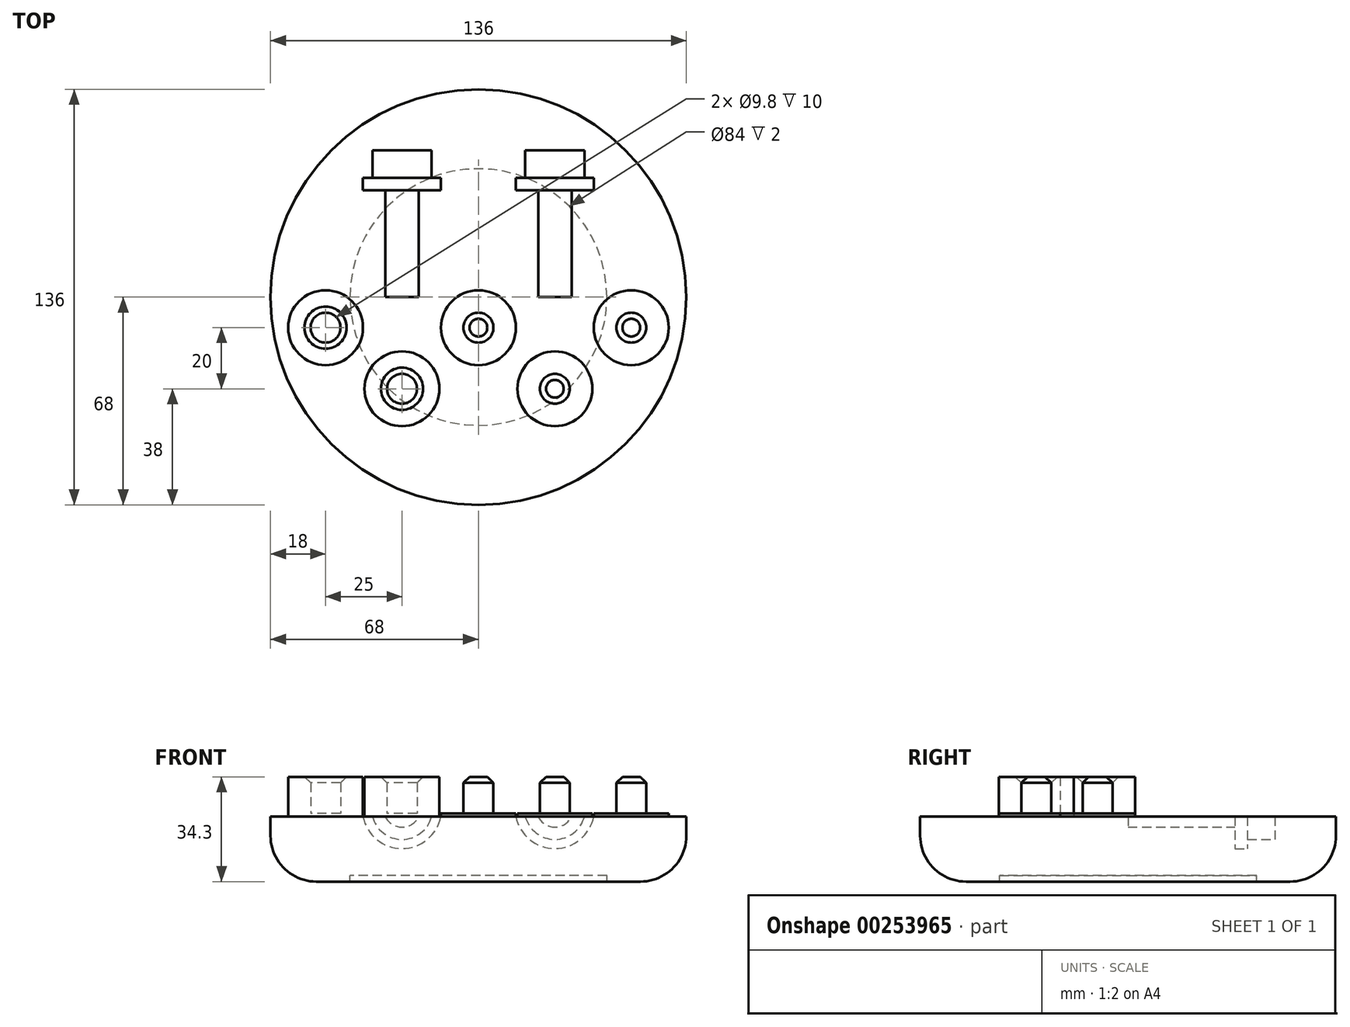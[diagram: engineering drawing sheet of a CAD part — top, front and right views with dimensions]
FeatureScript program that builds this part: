
annotation { "Feature Type Name" : "Feature", "Feature Type Description" : "" }
export const myFeature = defineFeature(function(context is Context, id is Id, definition is map)
    precondition{}
    {
        {
            var Q0;
            Q0=qCreatedBy(makeId("Front.planeOp"),FACE);
            var sketch = newSketch(context, id + "F0", { "sketchPlane" : qUnion([Q0])});
            skLineSegment(sketch, "E0.bottom", {"start": v(0, 0) * mm, "end": v(-68, 0) * mm});
            skLineSegment(sketch, "E0.top", {"start": v(-42, -21.3) * mm, "end": v(-53, -21.3) * mm});
            skLineSegment(sketch, "E0.left", {"start": v(0, 0) * mm, "end": v(0, -19.3) * mm});
            skLineSegment(sketch, "E0.right", {"start": v(-68, 0) * mm, "end": v(-68, -6.3) * mm});
            skLineSegment(sketch, "E1.top", {"start": v(0, -19.3) * mm, "end": v(-42, -19.3) * mm});
            skLineSegment(sketch, "E1.right", {"start": v(-42, -21.3) * mm, "end": v(-42, -19.3) * mm});
            skPoint(sketch, "E2.visualSharp", {"position": v(-68, -21.3) * mm});
            skArc(sketch, "E2.filletArc", {"start": v(-68, -6.3) * mm, "mid": v(-63.6, -16.9) * mm, "end": v(-53, -21.3) * mm});
            skSolve(sketch);
        }
        {
            var Q0;
            Q0=makeQuery(id+"F0.imprint","IMPRINT",FACE,{"disambiguationData":[TD([[makeQuery(id+"F0.imprint","IMPRINT",EDGE,{"derivedFrom":sQuery(id+"F0.wireOp",EDGE,"E0.bottom")}),1.0]])]});
            var Q1;
            Q1=sQuery(id+"F0.wireOp",EDGE,"E0.left");
            revolve(context, id + "F1", {"entities" : qUnion([Q0]), "axis" : qUnion([Q1]), "revolveType" : RevolveType.FULL});
        }
        {
            var Q0;
            Q0=makeQuery(id+"F1.opRevolve","SWEPT_FACE",FACE,{"disambiguationData":[OSD([sQuery(id+"F0.wireOp",EDGE,"E0.bottom")])]});
            var sketch = newSketch(context, id + "F2", { "sketchPlane" : qUnion([Q0])});
            skLineSegment(sketch, "E3.bottom", {"start": v(0, 0) * mm, "end": v(50, 0) * mm, "construction": true});
            skLineSegment(sketch, "E3.top", {"start": v(0, -10) * mm, "end": v(50, -10) * mm, "construction": true});
            skLineSegment(sketch, "E3.left", {"start": v(0, 0) * mm, "end": v(0, -10) * mm, "construction": true});
            skLineSegment(sketch, "E3.right", {"start": v(50, 0) * mm, "end": v(50, -10) * mm, "construction": true});
            skLineSegment(sketch, "E4.bottom", {"start": v(0, 0) * mm, "end": v(25, 0) * mm, "construction": true});
            skLineSegment(sketch, "E4.top", {"start": v(0, -30) * mm, "end": v(25, -30) * mm, "construction": true});
            skLineSegment(sketch, "E4.left", {"start": v(0, 0) * mm, "end": v(0, -30) * mm, "construction": true});
            skLineSegment(sketch, "E4.right", {"start": v(25, 0) * mm, "end": v(25, -30) * mm, "construction": true});
            skCircle(sketch, "E5", {"center": v(25, -30) * mm, "radius": 4.9 * mm});
            skCircle(sketch, "E6", {"center": v(50, -10) * mm, "radius": 4.9 * mm});
            skCircle(sketch, "E7", {"center": v(0, -10) * mm, "radius": 4.9 * mm});
            skCircle(sketch, "E8.MirrorC", {"center": v(-25, -30) * mm, "radius": 4.9 * mm});
            skCircle(sketch, "E9.MirrorC", {"center": v(-50, -10) * mm, "radius": 4.9 * mm});
            skCircle(sketch, "E10", {"center": v(0, -10) * mm, "radius": 12.25 * mm});
            skCircle(sketch, "E11", {"center": v(25, -30) * mm, "radius": 12.25 * mm});
            skCircle(sketch, "E12", {"center": v(50, -10) * mm, "radius": 12.25 * mm});
            skCircle(sketch, "E13", {"center": v(-25, -30) * mm, "radius": 12.25 * mm});
            skCircle(sketch, "E14", {"center": v(-50, -10) * mm, "radius": 12.25 * mm});
            skSolve(sketch);
        }
        {
            var Q0;
            Q0=makeQuery(id+"F2.imprint","IMPRINT",FACE,{"disambiguationData":[TD([[makeQuery(id+"F2.imprint","IMPRINT",EDGE,{"derivedFrom":sQuery(id+"F2.wireOp",EDGE,"E9.MirrorC")}),-1.0]])]});
            var Q1;
            Q1=makeQuery(id+"F2.imprint","IMPRINT",FACE,{"disambiguationData":[TD([[makeQuery(id+"F2.imprint","IMPRINT",EDGE,{"derivedFrom":sQuery(id+"F2.wireOp",EDGE,"E8.MirrorC")}),-1.0]])]});
            var Q2;
            Q2=makeQuery(id+"F2.imprint","IMPRINT",FACE,{"disambiguationData":[TD([[makeQuery(id+"F2.imprint","IMPRINT",EDGE,{"derivedFrom":sQuery(id+"F2.wireOp",EDGE,"E7")}),1.0]])]});
            var Q3;
            Q3=makeQuery(id+"F2.imprint","IMPRINT",FACE,{"disambiguationData":[TD([[makeQuery(id+"F2.imprint","IMPRINT",EDGE,{"derivedFrom":sQuery(id+"F2.wireOp",EDGE,"E5")}),1.0]])]});
            var Q4;
            Q4=makeQuery(id+"F2.imprint","IMPRINT",FACE,{"disambiguationData":[TD([[makeQuery(id+"F2.imprint","IMPRINT",EDGE,{"derivedFrom":sQuery(id+"F2.wireOp",EDGE,"E6")}),1.0]])]});
            extrude(context, id + "F3", {"entities" : qUnion([Q0, Q1, Q2, Q3, Q4]), "operationType" : NewBodyOperationType.ADD, "depth" : 13 * mm});
        }
        {
            var Q0;
            Q0=makeQuery(id+"F2.imprint","IMPRINT",FACE,{"disambiguationData":[TD([[makeQuery(id+"F2.imprint","IMPRINT",EDGE,{"derivedFrom":sQuery(id+"F2.wireOp",EDGE,"E9.MirrorC")}),1.0]])]});
            var Q1;
            Q1=makeQuery(id+"F2.imprint","IMPRINT",FACE,{"disambiguationData":[TD([[makeQuery(id+"F2.imprint","IMPRINT",EDGE,{"derivedFrom":sQuery(id+"F2.wireOp",EDGE,"E8.MirrorC")}),1.0]])]});
            var Q2;
            Q2=makeQuery(id+"F2.imprint","IMPRINT",FACE,{"disambiguationData":[TD([[makeQuery(id+"F2.imprint","IMPRINT",EDGE,{"derivedFrom":sQuery(id+"F2.wireOp",EDGE,"E7")}),-1.0]])]});
            var Q3;
            Q3=makeQuery(id+"F2.imprint","IMPRINT",FACE,{"disambiguationData":[TD([[makeQuery(id+"F2.imprint","IMPRINT",EDGE,{"derivedFrom":sQuery(id+"F2.wireOp",EDGE,"E5")}),-1.0]])]});
            var Q4;
            Q4=makeQuery(id+"F2.imprint","IMPRINT",FACE,{"disambiguationData":[TD([[makeQuery(id+"F2.imprint","IMPRINT",EDGE,{"derivedFrom":sQuery(id+"F2.wireOp",EDGE,"E6")}),-1.0]])]});
            extrude(context, id + "F4", {"entities" : qUnion([Q0, Q1, Q2, Q3, Q4]), "operationType" : NewBodyOperationType.ADD, "depth" : 1 * mm});
        }
        {
            var Q0;
            Q0=makeQuery(id+"F3.opExtrude","CAP_EDGE",EDGE,{"disambiguationData":[OSD([sQuery(id+"F2.wireOp",EDGE,"E9.MirrorC")])],"isStart":false});
            var Q1;
            Q1=makeQuery(id+"F3.opExtrude","CAP_EDGE",EDGE,{"disambiguationData":[OSD([sQuery(id+"F2.wireOp",EDGE,"E8.MirrorC")])],"isStart":false});
            var Q2;
            Q2=makeQuery(id+"F3.opExtrude","CAP_EDGE",EDGE,{"disambiguationData":[OSD([sQuery(id+"F2.wireOp",EDGE,"E7")])],"isStart":false});
            var Q3;
            Q3=makeQuery(id+"F3.opExtrude","CAP_EDGE",EDGE,{"disambiguationData":[OSD([sQuery(id+"F2.wireOp",EDGE,"E5")])],"isStart":false});
            var Q4;
            Q4=makeQuery(id+"F3.opExtrude","CAP_EDGE",EDGE,{"disambiguationData":[OSD([sQuery(id+"F2.wireOp",EDGE,"E6")])],"isStart":false});
            chamfer(context, id + "F5", {"entities" : qUnion([Q0, Q1, Q2, Q3, Q4]), "width" : 2 * mm, "tangentPropagation" : true});
        }
        {
            var Q0;
            Q0=makeQuery(id+"F1.opRevolve","SWEPT_FACE",FACE,{"disambiguationData":[OSD([sQuery(id+"F0.wireOp",EDGE,"E0.bottom")])]});
            cPlane(context, id + "F6", {"entities" : qUnion([Q0]), "cplaneType" : CPlaneType.OFFSET, "offset" : 2.5 * mm, "width" : 150 * mm, "height" : 150 * mm});
        }
        {
            var Q0;
            Q0=qCreatedBy(id+"F6.planeOp",FACE);
            var sketch = newSketch(context, id + "F7", { "sketchPlane" : qUnion([Q0])});
            skLineSegment(sketch, "E15", {"start": v(0, 0) * mm, "end": v(25, 0) * mm, "construction": true});
            skLineSegment(sketch, "E16", {"start": v(0, 0) * mm, "end": v(0, 15) * mm, "construction": true});
            skLineSegment(sketch, "E17.bottom", {"start": v(25, 0) * mm, "end": v(31, 0) * mm});
            skLineSegment(sketch, "E17.left", {"start": v(25, 0) * mm, "end": v(25, 35) * mm});
            skLineSegment(sketch, "E17.right", {"start": v(31, 0) * mm, "end": v(31, 35) * mm});
            skLineSegment(sketch, "E18.bottom", {"start": v(31, 35) * mm, "end": v(38, 35) * mm});
            skLineSegment(sketch, "E18.top", {"start": v(35, 39) * mm, "end": v(38, 39) * mm});
            skLineSegment(sketch, "E18.left", {"start": v(25, 35) * mm, "end": v(25, 39) * mm});
            skLineSegment(sketch, "E18.right", {"start": v(38, 35) * mm, "end": v(38, 39) * mm});
            skLineSegment(sketch, "E19.top", {"start": v(25, 48) * mm, "end": v(35, 48) * mm});
            skLineSegment(sketch, "E19.left", {"start": v(25, 39) * mm, "end": v(25, 48) * mm});
            skLineSegment(sketch, "E19.right", {"start": v(35, 39) * mm, "end": v(35, 48) * mm});
            skLineSegment(sketch, "E20.MirrorCS", {"start": v(-25, 0) * mm, "end": v(-25, 35) * mm});
            skLineSegment(sketch, "E21.MirrorCS", {"start": v(-25, 35) * mm, "end": v(-25, 39) * mm});
            skLineSegment(sketch, "E22.MirrorCS", {"start": v(-25, 39) * mm, "end": v(-25, 48) * mm});
            skLineSegment(sketch, "E23.MirrorCS", {"start": v(-25, 48) * mm, "end": v(-35, 48) * mm});
            skLineSegment(sketch, "E24.MirrorCS", {"start": v(-35, 39) * mm, "end": v(-35, 48) * mm});
            skLineSegment(sketch, "E25.MirrorCS", {"start": v(-35, 39) * mm, "end": v(-38, 39) * mm});
            skLineSegment(sketch, "E26.MirrorCS", {"start": v(-38, 35) * mm, "end": v(-38, 39) * mm});
            skLineSegment(sketch, "E27.MirrorCS", {"start": v(-31, 35) * mm, "end": v(-38, 35) * mm});
            skLineSegment(sketch, "E28.MirrorCS", {"start": v(-31, 0) * mm, "end": v(-31, 35) * mm});
            skLineSegment(sketch, "E29.MirrorCS", {"start": v(-25, 0) * mm, "end": v(-31, 0) * mm});
            skSolve(sketch);
        }
        {
            var Q0;
            Q0=makeQuery(id+"F7.imprint","IMPRINT",FACE,{"disambiguationData":[TD([[makeQuery(id+"F7.imprint","IMPRINT",EDGE,{"derivedFrom":sQuery(id+"F7.wireOp",EDGE,"E20.MirrorCS")}),1.0]])]});
            var Q1;
            Q1=sQuery(id+"F7.wireOp",EDGE,"E20.MirrorCS");
            revolve(context, id + "F8", {"operationType" : NewBodyOperationType.REMOVE, "entities" : qUnion([Q0]), "axis" : qUnion([Q1]), "revolveType" : RevolveType.FULL, "oppositeDirection" : true});
        }
        {
            var Q0;
            Q0=makeQuery(id+"F7.imprint","IMPRINT",FACE,{"disambiguationData":[TD([[makeQuery(id+"F7.imprint","IMPRINT",EDGE,{"derivedFrom":sQuery(id+"F7.wireOp",EDGE,"E17.bottom")}),1.0]])]});
            var Q1;
            Q1=sQuery(id+"F7.wireOp",EDGE,"E17.left");
            revolve(context, id + "F9", {"operationType" : NewBodyOperationType.REMOVE, "entities" : qUnion([Q0]), "axis" : qUnion([Q1]), "revolveType" : RevolveType.FULL, "oppositeDirection" : true});
        }
    });
